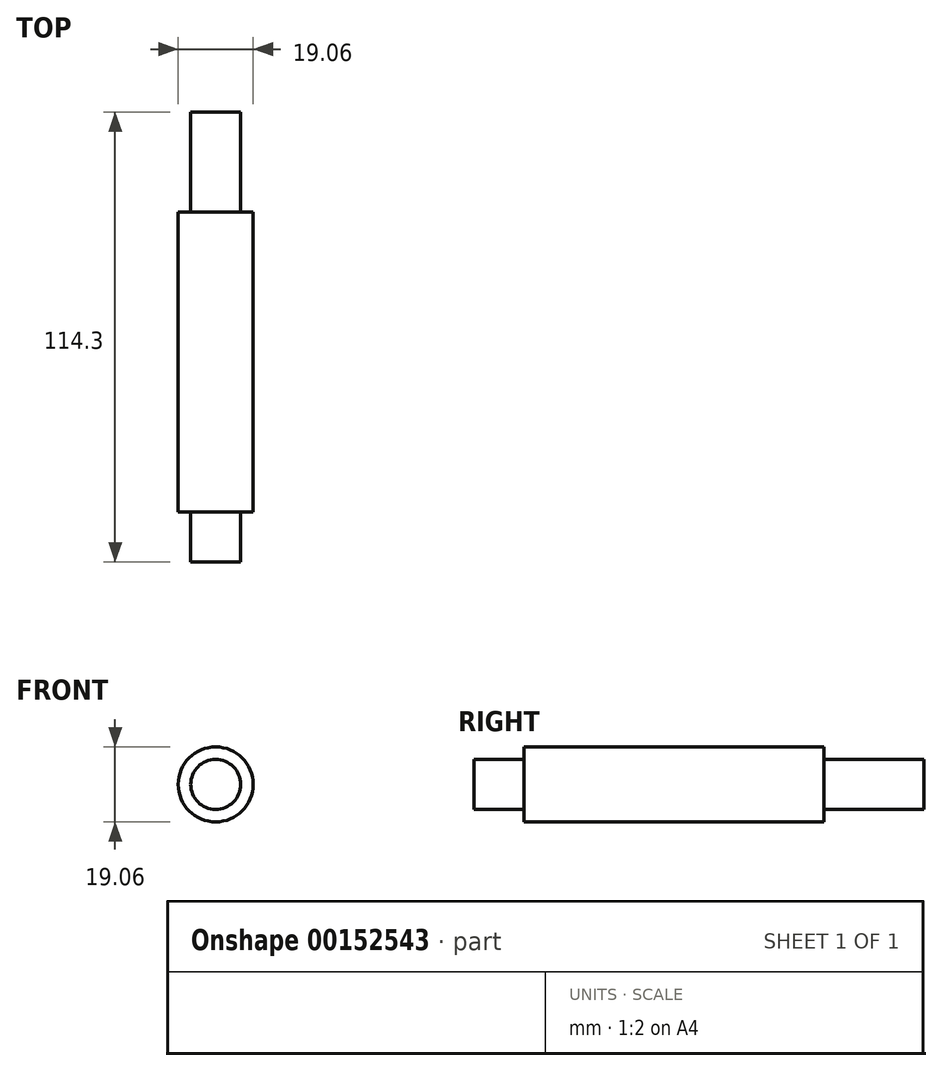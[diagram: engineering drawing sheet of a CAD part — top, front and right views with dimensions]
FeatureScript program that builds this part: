
annotation { "Feature Type Name" : "Feature", "Feature Type Description" : "" }
export const myFeature = defineFeature(function(context is Context, id is Id, definition is map)
    precondition{}
    {
        {
            var Q0;
            Q0=qCreatedBy(makeId("Front.planeOp"),FACE);
            var sketch = newSketch(context, id + "F0", { "sketchPlane" : qUnion([Q0])});
            skCircle(sketch, "E0", {"center": v(0, 0) * mm, "radius": 6.35 * mm});
            skSolve(sketch);
        }
        {
            var Q0;
            Q0 = qSketchRegion(id + "F0", true);
            extrude(context, id + "F1", {"entities" : qUnion([Q0]), "depth" : 25.4 * mm});
        }
        {
            var Q0;
            Q0=makeQuery(id+"F1.opExtrude","CAP_FACE",FACE,{"disambiguationData":[OSD([sQuery(id+"F0.wireOp",EDGE,"E0")])],"isStart":false});
            var sketch = newSketch(context, id + "F2", { "sketchPlane" : qUnion([Q0])});
            skCircle(sketch, "E1", {"center": v(0, 0) * mm, "radius": 9.53 * mm});
            skSolve(sketch);
        }
        {
            var Q0;
            Q0 = qSketchRegion(id + "F2", true);
            extrude(context, id + "F3", {"entities" : qUnion([Q0]), "operationType" : NewBodyOperationType.ADD, "depth" : 76.2 * mm});
        }
        {
            var Q0;
            Q0=makeQuery(id+"F3.opExtrude","CAP_FACE",FACE,{"disambiguationData":[OSD([sQuery(id+"F2.wireOp",EDGE,"E1")])],"isStart":false});
            var sketch = newSketch(context, id + "F4", { "sketchPlane" : qUnion([Q0])});
            skCircle(sketch, "E2", {"center": v(0, 0) * mm, "radius": 6.35 * mm});
            skSolve(sketch);
        }
        {
            var Q0;
            Q0 = qSketchRegion(id + "F4", true);
            extrude(context, id + "F5", {"entities" : qUnion([Q0]), "operationType" : NewBodyOperationType.ADD, "depth" : 12.7 * mm});
        }
    });
